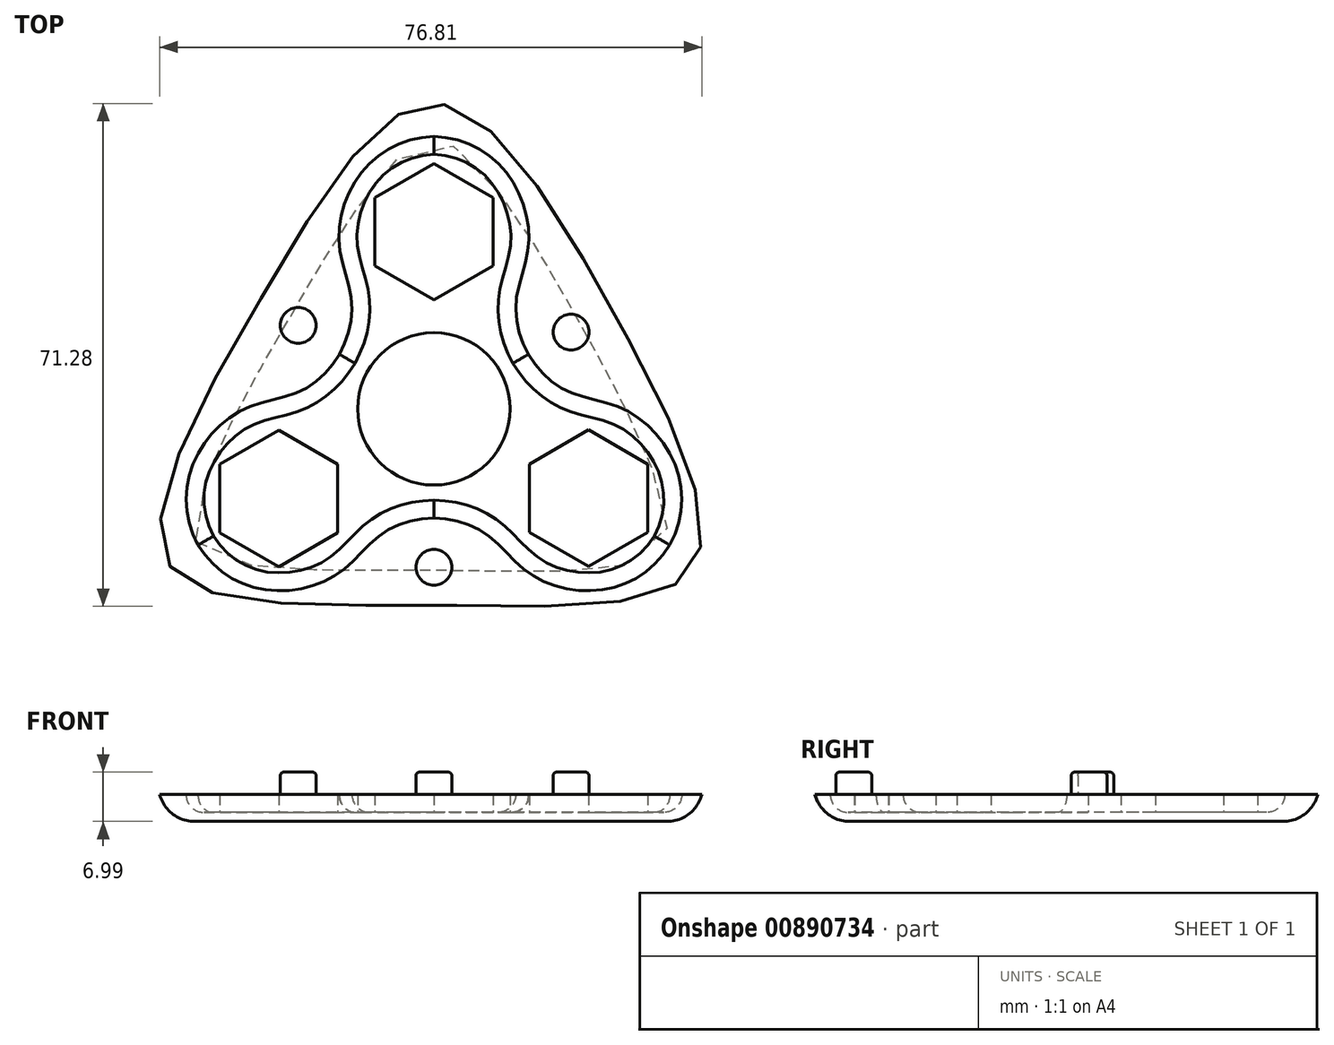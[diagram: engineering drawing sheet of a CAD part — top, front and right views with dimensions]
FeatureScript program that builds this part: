
annotation { "Feature Type Name" : "Feature", "Feature Type Description" : "" }
export const myFeature = defineFeature(function(context is Context, id is Id, definition is map)
    precondition{}
    {
        {
            var Q0;
            Q0=qCreatedBy(makeId("Top.planeOp"),FACE);
            var sketch = newSketch(context, id + "F0", { "sketchPlane" : qUnion([Q0])});
            skCircle(sketch, "E0", {"center": v(0, 0) * mm, "radius": 10.8 * mm});
            skLineSegment(sketch, "E1", {"start": v(0, 0) * mm, "end": v(0, 25.1) * mm, "construction": true});
            skLineSegment(sketch, "E2", {"start": v(0, 0) * mm, "end": v(21.74, 12.55) * mm, "construction": true});
            skLineSegment(sketch, "E3", {"start": v(0, 0) * mm, "end": v(21.94, -12.67) * mm, "construction": true});
            skLineSegment(sketch, "E4", {"start": v(0, 0) * mm, "end": v(0, -25.1) * mm, "construction": true});
            skLineSegment(sketch, "E5", {"start": v(0, 0) * mm, "end": v(-22, -12.7) * mm, "construction": true});
            skLineSegment(sketch, "E6", {"start": v(0, 0) * mm, "end": v(-21.74, 12.55) * mm, "construction": true});
            skCircle(sketch, "E7.cCircle", {"center": v(0, 25.1) * mm, "radius": 8.38 * mm, "construction": true});
            skLineSegment(sketch, "E7.0", {"start": v(8.38, 29.95) * mm, "end": v(8.38, 20.27) * mm});
            skLineSegment(sketch, "E7.1", {"start": v(8.38, 20.27) * mm, "end": v(0, 15.43) * mm});
            skLineSegment(sketch, "E7.2", {"start": v(0, 15.43) * mm, "end": v(-8.38, 20.27) * mm});
            skLineSegment(sketch, "E7.3", {"start": v(-8.38, 20.27) * mm, "end": v(-8.38, 29.95) * mm});
            skLineSegment(sketch, "E7.4", {"start": v(-8.38, 29.95) * mm, "end": v(0, 34.79) * mm});
            skLineSegment(sketch, "E7.5", {"start": v(0, 34.79) * mm, "end": v(8.38, 29.95) * mm});
            skPoint(sketch, "E7.0.midPoint", {"position": v(8.38, 25.1) * mm});
            skCircle(sketch, "E8.cCircle", {"center": v(21.94, -12.67) * mm, "radius": 8.38 * mm, "construction": true});
            skLineSegment(sketch, "E8.0", {"start": v(13.55, -17.5) * mm, "end": v(13.55, -7.83) * mm});
            skLineSegment(sketch, "E8.1", {"start": v(13.55, -7.83) * mm, "end": v(21.94, -2.99) * mm});
            skLineSegment(sketch, "E8.2", {"start": v(21.94, -2.99) * mm, "end": v(30.32, -7.83) * mm});
            skLineSegment(sketch, "E8.3", {"start": v(30.32, -7.83) * mm, "end": v(30.32, -17.5) * mm});
            skLineSegment(sketch, "E8.4", {"start": v(30.32, -17.5) * mm, "end": v(21.94, -22.34) * mm});
            skLineSegment(sketch, "E8.5", {"start": v(21.94, -22.34) * mm, "end": v(13.55, -17.5) * mm});
            skPoint(sketch, "E8.0.midPoint", {"position": v(13.55, -12.67) * mm});
            skCircle(sketch, "E9.cCircle", {"center": v(-22, -12.7) * mm, "radius": 8.38 * mm, "construction": true});
            skLineSegment(sketch, "E9.0", {"start": v(-13.6, -7.86) * mm, "end": v(-13.6, -17.54) * mm});
            skLineSegment(sketch, "E9.1", {"start": v(-13.6, -17.54) * mm, "end": v(-22, -22.38) * mm});
            skLineSegment(sketch, "E9.2", {"start": v(-22, -22.38) * mm, "end": v(-30.37, -17.54) * mm});
            skLineSegment(sketch, "E9.3", {"start": v(-30.37, -17.54) * mm, "end": v(-30.37, -7.86) * mm});
            skLineSegment(sketch, "E9.4", {"start": v(-30.37, -7.86) * mm, "end": v(-22, -3.02) * mm});
            skLineSegment(sketch, "E9.5", {"start": v(-22, -3.02) * mm, "end": v(-13.6, -7.86) * mm});
            skPoint(sketch, "E9.0.midPoint", {"position": v(-13.6, -12.7) * mm});
            skFitSpline(sketch, "E10", {"points": [v(0, 38.6) * mm, v(13.45, 23.73) * mm, v(13.39, 7.73) * mm], "startDerivative": vector(54.84, -2.13) * mm, "endDerivative": vector(24.96, -47.54) * mm});
            skFitSpline(sketch, "E11.MirrorCS", {"points": [v(33.44, -19.3) * mm, v(27.28, -0.22) * mm, v(13.39, 7.73) * mm], "startDerivative": vector(25.58, 48.55) * mm, "endDerivative": vector(-28.7, 45.38) * mm});
            skFitSpline(sketch, "E12.MirrorCS", {"points": [v(33.44, -19.3) * mm, v(13.83, -23.51) * mm, v(0, -15.46) * mm], "startDerivative": vector(-29.26, -46.43) * mm, "endDerivative": vector(-53.65, 2.16) * mm});
            skFitSpline(sketch, "E13.MirrorCS", {"points": [v(-33.44, -19.3) * mm, v(-13.83, -23.51) * mm, v(0, -15.46) * mm], "startDerivative": vector(29.26, -46.43) * mm, "endDerivative": vector(53.65, 2.16) * mm});
            skFitSpline(sketch, "E14.MirrorCS", {"points": [v(-33.44, -19.3) * mm, v(-27.28, -0.22) * mm, v(-13.39, 7.73) * mm], "startDerivative": vector(-25.58, 48.55) * mm, "endDerivative": vector(28.7, 45.38) * mm});
            skFitSpline(sketch, "E15.MirrorCS", {"points": [v(0, 38.6) * mm, v(-13.45, 23.73) * mm, v(-13.39, 7.73) * mm], "startDerivative": vector(-54.84, -2.13) * mm, "endDerivative": vector(-24.96, -47.54) * mm});
            skSolve(sketch);
        }
        {
            var Q0;
            Q0=makeQuery(id+"F0.imprint","IMPRINT",FACE,{"disambiguationData":[TD([[makeQuery(id+"F0.imprint","IMPRINT",EDGE,{"derivedFrom":sQuery(id+"F0.wireOp",EDGE,"E0")}),-1.0]])]});
            extrude(context, id + "F1", {"entities" : qUnion([Q0]), "endBound" : BoundingType.SYMMETRIC, "depth" : 5.08 * mm, "offsetDistance" : 25.4 * mm});
        }
        {
            var Q0;
            Q0=makeQuery(id+"F1.opExtrude","CAP_EDGE",EDGE,{"disambiguationData":[OSD([sQuery(id+"F0.wireOp",EDGE,"E13.MirrorCS")])],"isStart":false});
            var Q1;
            Q1=makeQuery(id+"F1.opExtrude","CAP_EDGE",EDGE,{"disambiguationData":[OSD([sQuery(id+"F0.wireOp",EDGE,"E12.MirrorCS")])],"isStart":false});
            var Q2;
            Q2=makeQuery(id+"F1.opExtrude","CAP_EDGE",EDGE,{"disambiguationData":[OSD([sQuery(id+"F0.wireOp",EDGE,"E11.MirrorCS")])],"isStart":false});
            var Q3;
            Q3=makeQuery(id+"F1.opExtrude","CAP_EDGE",EDGE,{"disambiguationData":[OSD([sQuery(id+"F0.wireOp",EDGE,"E10")])],"isStart":false});
            var Q4;
            Q4=makeQuery(id+"F1.opExtrude","CAP_EDGE",EDGE,{"disambiguationData":[OSD([sQuery(id+"F0.wireOp",EDGE,"E15.MirrorCS")])],"isStart":false});
            var Q5;
            Q5=makeQuery(id+"F1.opExtrude","CAP_EDGE",EDGE,{"disambiguationData":[OSD([sQuery(id+"F0.wireOp",EDGE,"E14.MirrorCS")])],"isStart":false});
            var Q6;
            Q6=makeQuery(id+"F1.opExtrude","CAP_EDGE",EDGE,{"disambiguationData":[OSD([sQuery(id+"F0.wireOp",EDGE,"E13.MirrorCS")])],"isStart":true});
            var Q7;
            Q7=makeQuery(id+"F1.opExtrude","CAP_EDGE",EDGE,{"disambiguationData":[OSD([sQuery(id+"F0.wireOp",EDGE,"E12.MirrorCS")])],"isStart":true});
            var Q8;
            Q8=makeQuery(id+"F1.opExtrude","CAP_EDGE",EDGE,{"disambiguationData":[OSD([sQuery(id+"F0.wireOp",EDGE,"E11.MirrorCS")])],"isStart":true});
            var Q9;
            Q9=makeQuery(id+"F1.opExtrude","CAP_EDGE",EDGE,{"disambiguationData":[OSD([sQuery(id+"F0.wireOp",EDGE,"E10")])],"isStart":true});
            var Q10;
            Q10=makeQuery(id+"F1.opExtrude","CAP_EDGE",EDGE,{"disambiguationData":[OSD([sQuery(id+"F0.wireOp",EDGE,"E15.MirrorCS")])],"isStart":true});
            var Q11;
            Q11=makeQuery(id+"F1.opExtrude","CAP_EDGE",EDGE,{"disambiguationData":[OSD([sQuery(id+"F0.wireOp",EDGE,"E14.MirrorCS")])],"isStart":true});
            fillet(context, id + "F2", {"entities" : qUnion([Q0, Q1, Q2, Q3, Q4, Q5, Q6, Q7, Q8, Q9, Q10, Q11]), "radius" : 2.54 * mm, "tangentPropagation" : true, "allowEdgeOverflow" : false});
        }
        {
            var Q0;
            Q0=qCreatedBy(makeId("Top.planeOp"),FACE);
            var sketch = newSketch(context, id + "F3", { "sketchPlane" : qUnion([Q0])});
            skFitSpline(sketch, "E16", {"points": [v(-24.52, 15.68) * mm, v(0, 43.3) * mm, v(25.1, 14.34) * mm, v(36.7, -22.45) * mm, v(0, -27.82) * mm, v(-37.72, -21.83) * mm, v(-24.52, 15.68) * mm]});
            skCircle(sketch, "E17", {"center": v(-19.23, 11.83) * mm, "radius": 2.54 * mm});
            skCircle(sketch, "E18", {"center": v(19.44, 10.89) * mm, "radius": 2.54 * mm});
            skCircle(sketch, "E19", {"center": v(0, -22.45) * mm, "radius": 2.54 * mm});
            skSolve(sketch);
        }
        {
            var Q0;
            Q0=makeQuery(id+"F3.imprint","IMPRINT",FACE,{"disambiguationData":[TD([[makeQuery(id+"F3.imprint","IMPRINT",EDGE,{"derivedFrom":sQuery(id+"F3.wireOp",EDGE,"E16")}),-1.0]])]});
            var Q1;
            Q1=makeQuery(id+"F3.imprint","IMPRINT",FACE,{"disambiguationData":[TD([[makeQuery(id+"F3.imprint","IMPRINT",EDGE,{"derivedFrom":sQuery(id+"F3.wireOp",EDGE,"E17")}),1.0]])]});
            var Q2;
            Q2=makeQuery(id+"F3.imprint","IMPRINT",FACE,{"disambiguationData":[TD([[makeQuery(id+"F3.imprint","IMPRINT",EDGE,{"derivedFrom":sQuery(id+"F3.wireOp",EDGE,"E18")}),1.0]])]});
            var Q3;
            Q3=makeQuery(id+"F3.imprint","IMPRINT",FACE,{"disambiguationData":[TD([[makeQuery(id+"F3.imprint","IMPRINT",EDGE,{"derivedFrom":sQuery(id+"F3.wireOp",EDGE,"E19")}),1.0]])]});
            extrude(context, id + "F4", {"entities" : qUnion([Q0, Q1, Q2, Q3]), "oppositeDirection" : true, "depth" : 3.8 * mm, "offsetDistance" : 25.4 * mm});
        }
        {
            var Q0;
            Q0=makeQuery(id+"F3.imprint","IMPRINT",FACE,{"disambiguationData":[TD([[makeQuery(id+"F3.imprint","IMPRINT",EDGE,{"derivedFrom":sQuery(id+"F3.wireOp",EDGE,"E17")}),1.0]])]});
            var Q1;
            Q1=makeQuery(id+"F3.imprint","IMPRINT",FACE,{"disambiguationData":[TD([[makeQuery(id+"F3.imprint","IMPRINT",EDGE,{"derivedFrom":sQuery(id+"F3.wireOp",EDGE,"E18")}),1.0]])]});
            var Q2;
            Q2=makeQuery(id+"F3.imprint","IMPRINT",FACE,{"disambiguationData":[TD([[makeQuery(id+"F3.imprint","IMPRINT",EDGE,{"derivedFrom":sQuery(id+"F3.wireOp",EDGE,"E19")}),1.0]])]});
            extrude(context, id + "F5", {"entities" : qUnion([Q0, Q1, Q2]), "operationType" : NewBodyOperationType.ADD, "depth" : 3.17 * mm, "offsetDistance" : 25.4 * mm});
        }
        {
            var Q0;
            Q0=makeQuery(id+"F1.opExtrude","SWEPT_BODY",BODY,{"disambiguationData":[OSD([sQuery(id+"F0.wireOp",EDGE,"E0"),sQuery(id+"F0.wireOp",EDGE,"E7.0"),sQuery(id+"F0.wireOp",EDGE,"E7.1"),sQuery(id+"F0.wireOp",EDGE,"E7.2"),sQuery(id+"F0.wireOp",EDGE,"E7.3"),sQuery(id+"F0.wireOp",EDGE,"E7.4"),sQuery(id+"F0.wireOp",EDGE,"E7.5"),sQuery(id+"F0.wireOp",EDGE,"E8.0"),sQuery(id+"F0.wireOp",EDGE,"E8.1"),sQuery(id+"F0.wireOp",EDGE,"E8.2"),sQuery(id+"F0.wireOp",EDGE,"E8.3"),sQuery(id+"F0.wireOp",EDGE,"E8.4"),sQuery(id+"F0.wireOp",EDGE,"E8.5"),sQuery(id+"F0.wireOp",EDGE,"E9.0"),sQuery(id+"F0.wireOp",EDGE,"E9.1"),sQuery(id+"F0.wireOp",EDGE,"E9.2"),sQuery(id+"F0.wireOp",EDGE,"E9.3"),sQuery(id+"F0.wireOp",EDGE,"E9.4"),sQuery(id+"F0.wireOp",EDGE,"E9.5"),sQuery(id+"F0.wireOp",EDGE,"E10"),sQuery(id+"F0.wireOp",EDGE,"E11.MirrorCS"),sQuery(id+"F0.wireOp",EDGE,"E12.MirrorCS"),sQuery(id+"F0.wireOp",EDGE,"E13.MirrorCS"),sQuery(id+"F0.wireOp",EDGE,"E14.MirrorCS"),sQuery(id+"F0.wireOp",EDGE,"E15.MirrorCS")])]});
            var Q1;
            Q1=makeQuery(id+"F4.opExtrude","SWEPT_BODY",BODY,{"disambiguationData":[OSD([sQuery(id+"F3.wireOp",EDGE,"E16")])]});
            booleanBodies(context, id + "F6", {"operationType" : BooleanOperationType.SUBTRACTION, "tools" : qUnion([Q0]), "targets" : qUnion([Q1])});
        }
        {
            var Q0;
            Q0=makeQuery(id+"F5.opExtrude","CAP_EDGE",EDGE,{"disambiguationData":[OSD([sQuery(id+"F3.wireOp",EDGE,"E17")])],"isStart":false});
            var Q1;
            Q1=makeQuery(id+"F5.opExtrude","CAP_EDGE",EDGE,{"disambiguationData":[OSD([sQuery(id+"F3.wireOp",EDGE,"E19")])],"isStart":false});
            var Q2;
            Q2=makeQuery(id+"F5.opExtrude","CAP_EDGE",EDGE,{"disambiguationData":[OSD([sQuery(id+"F3.wireOp",EDGE,"E18")])],"isStart":false});
            fillet(context, id + "F7", {"entities" : qUnion([Q0, Q1, Q2]), "radius" : 0.5 * mm, "tangentPropagation" : true, "allowEdgeOverflow" : false});
        }
        {
            var Q0;
            Q0=makeQuery(id+"F4.opExtrude","CAP_EDGE",EDGE,{"disambiguationData":[OSD([sQuery(id+"F3.wireOp",EDGE,"E16")])],"isStart":false});
            fillet(context, id + "F8", {"entities" : qUnion([Q0]), "radius" : 5.08 * mm, "tangentPropagation" : true, "allowEdgeOverflow" : false});
        }
    });
